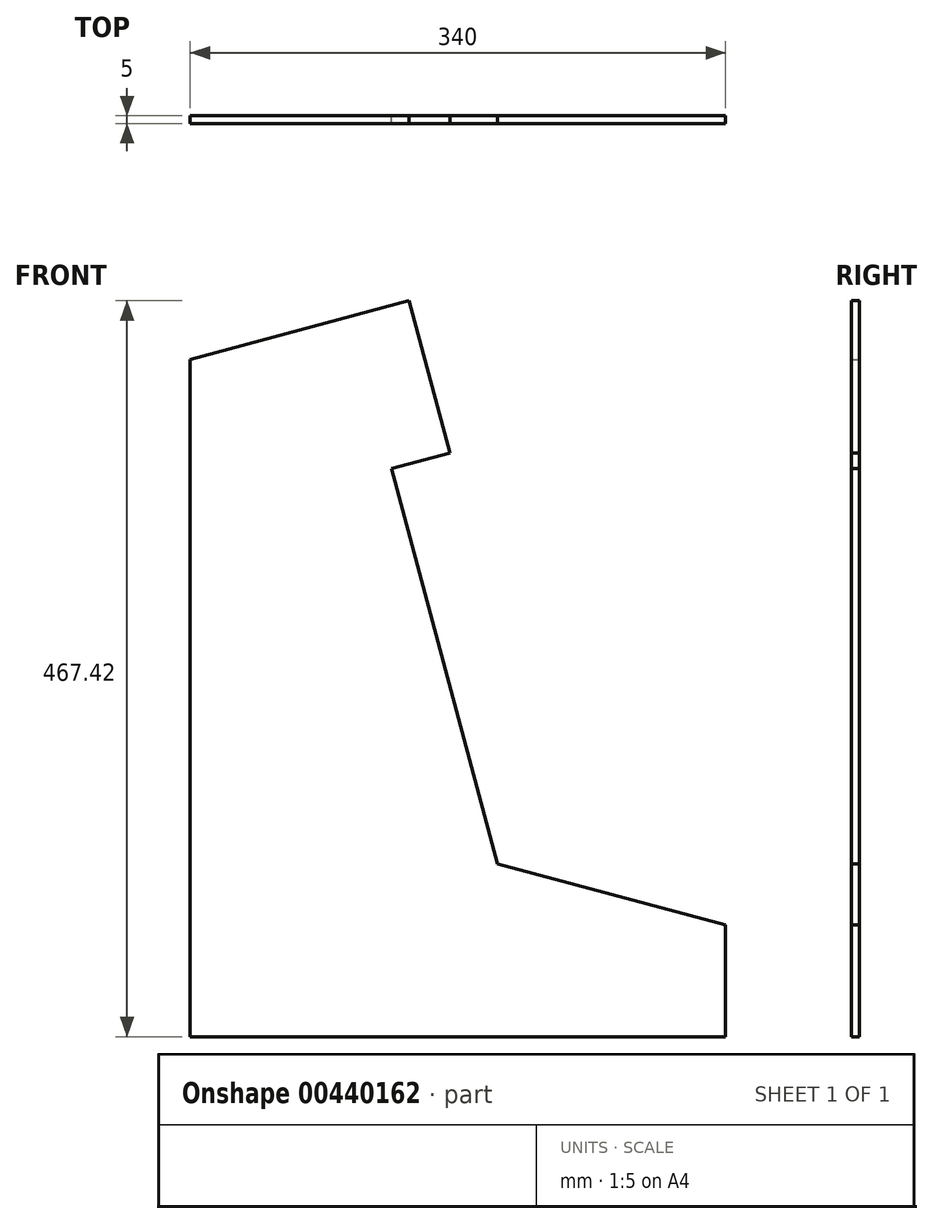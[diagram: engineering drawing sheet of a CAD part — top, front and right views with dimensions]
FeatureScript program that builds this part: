
annotation { "Feature Type Name" : "Feature", "Feature Type Description" : "" }
export const myFeature = defineFeature(function(context is Context, id is Id, definition is map)
    precondition{}
    {
        {
            var Q0;
            Q0=qCreatedBy(makeId("Front.planeOp"),FACE);
            var sketch = newSketch(context, id + "F0", { "sketchPlane" : qUnion([Q0])});
            skLineSegment(sketch, "E0", {"start": v(218.24, -245.17) * mm, "end": v(-121.76, -245.17) * mm});
            skLineSegment(sketch, "E1", {"start": v(-121.76, -245.17) * mm, "end": v(-121.76, 184.97) * mm});
            skLineSegment(sketch, "E2", {"start": v(-121.76, 184.97) * mm, "end": v(17.38, 222.25) * mm});
            skLineSegment(sketch, "E3", {"start": v(17.38, 222.25) * mm, "end": v(43.26, 125.66) * mm});
            skLineSegment(sketch, "E4", {"start": v(43.26, 125.66) * mm, "end": v(6.06, 115.69) * mm});
            skLineSegment(sketch, "E5", {"start": v(6.06, 115.69) * mm, "end": v(73.35, -135.45) * mm});
            skLineSegment(sketch, "E6", {"start": v(73.35, -135.45) * mm, "end": v(218.24, -174.28) * mm});
            skLineSegment(sketch, "E7", {"start": v(218.24, -174.28) * mm, "end": v(218.24, -245.17) * mm});
            skSolve(sketch);
        }
        {
            var Q0;
            Q0 = qSketchRegion(id + "F0", true);
            extrude(context, id + "F1", {"entities" : qUnion([Q0]), "depth" : 5 * mm});
        }
    });
